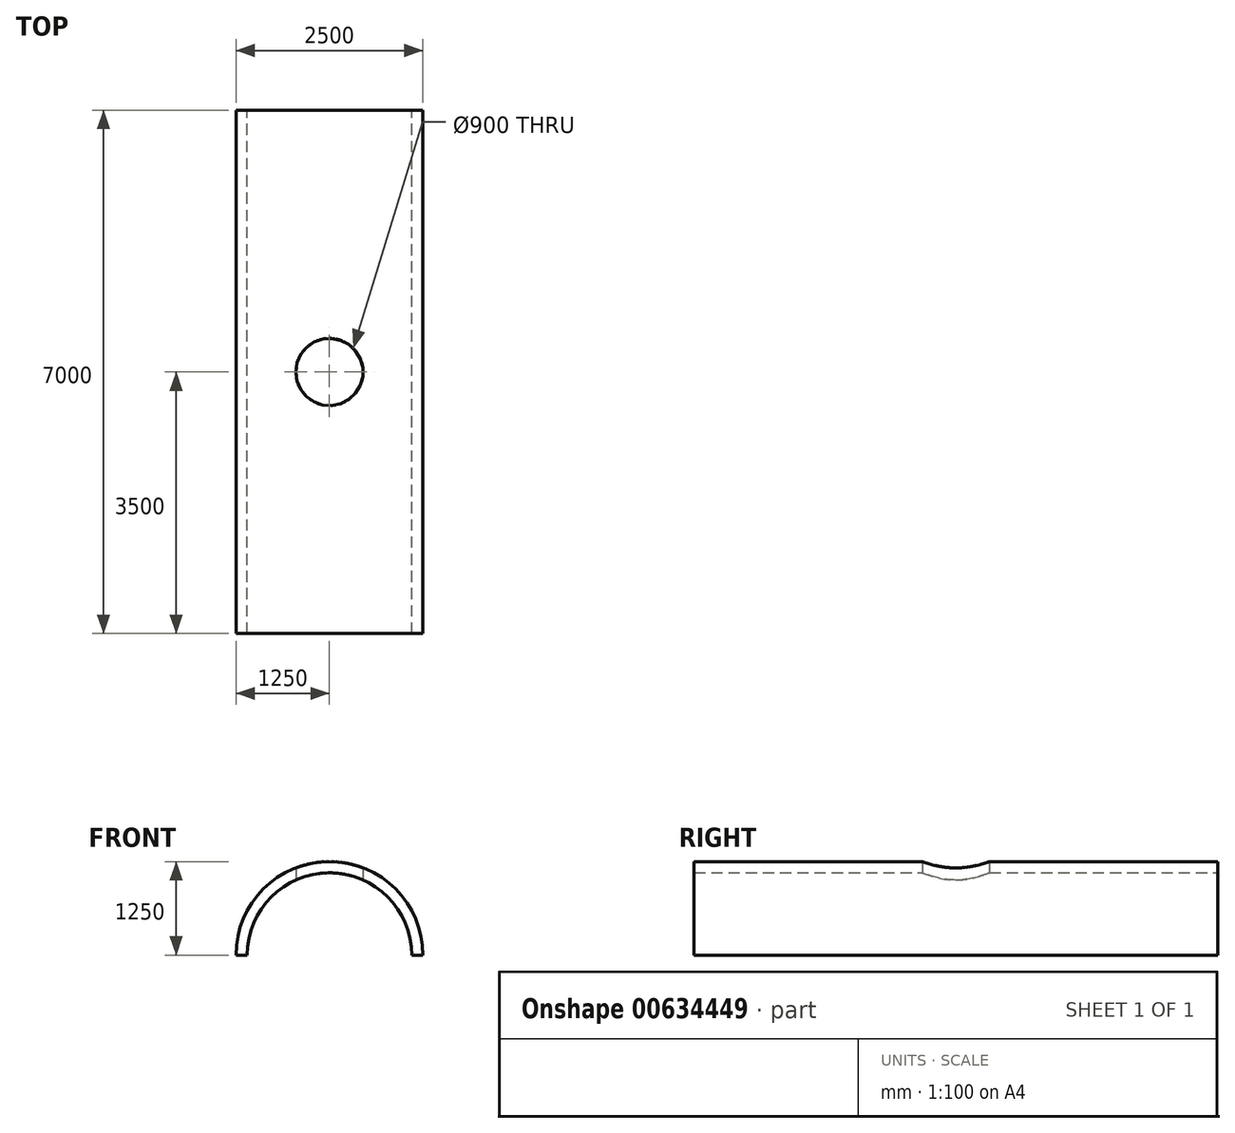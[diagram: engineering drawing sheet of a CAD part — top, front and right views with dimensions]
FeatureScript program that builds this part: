
annotation { "Feature Type Name" : "Feature", "Feature Type Description" : "" }
export const myFeature = defineFeature(function(context is Context, id is Id, definition is map)
    precondition{}
    {
        {
            var Q0;
            Q0=qCreatedBy(makeId("Front.planeOp"),FACE);
            var sketch = newSketch(context, id + "F0", { "sketchPlane" : qUnion([Q0])});
            skCircle(sketch, "E0", {"center": v(0, 0) * mm, "radius": 1250 * mm});
            skCircle(sketch, "E1", {"center": v(0, 0) * mm, "radius": 1100 * mm});
            skSolve(sketch);
        }
        {
            var Q0;
            Q0=makeQuery(id+"F0.imprint","IMPRINT",FACE,{"disambiguationData":[TD([[makeQuery(id+"F0.imprint","IMPRINT",EDGE,{"derivedFrom":sQuery(id+"F0.wireOp",EDGE,"E0")}),1.0]])]});
            extrude(context, id + "F1", {"entities" : qUnion([Q0]), "depth" : 7000 * mm, "offsetDistance" : 25 * mm});
        }
        {
            var Q0;
            Q0=qCreatedBy(makeId("Front.planeOp"),FACE);
            var sketch = newSketch(context, id + "F2", { "sketchPlane" : qUnion([Q0])});
            skLineSegment(sketch, "E2.bottom", {"start": v(-1995.14, 0) * mm, "end": v(2355.4, 0) * mm});
            skLineSegment(sketch, "E2.top", {"start": v(-1995.14, -1751.12) * mm, "end": v(2355.4, -1751.12) * mm});
            skLineSegment(sketch, "E2.left", {"start": v(-1995.14, 0) * mm, "end": v(-1995.14, -1751.12) * mm});
            skLineSegment(sketch, "E2.right", {"start": v(2355.4, 0) * mm, "end": v(2355.4, -1751.12) * mm});
            skSolve(sketch);
        }
        {
            var Q0;
            Q0=makeQuery(id+"F2.imprint","IMPRINT",FACE,{"disambiguationData":[TD([[makeQuery(id+"F2.imprint","IMPRINT",EDGE,{"derivedFrom":sQuery(id+"F2.wireOp",EDGE,"E2.bottom")}),-1.0]])]});
            extrude(context, id + "F3", {"entities" : qUnion([Q0]), "operationType" : NewBodyOperationType.REMOVE, "depth" : 8000 * mm, "offsetDistance" : 25 * mm});
        }
        {
            var Q0;
            Q0=qCreatedBy(makeId("Top.planeOp"),FACE);
            var sketch = newSketch(context, id + "F4", { "sketchPlane" : qUnion([Q0])});
            skCircle(sketch, "E3", {"center": v(0, -3500) * mm, "radius": 450 * mm});
            skSolve(sketch);
        }
        {
            var Q0;
            Q0=makeQuery(id+"F4.imprint","IMPRINT",FACE,{"disambiguationData":[TD([[makeQuery(id+"F4.imprint","IMPRINT",EDGE,{"derivedFrom":sQuery(id+"F4.wireOp",EDGE,"E3")}),1.0]])]});
            var Q1;
            Q1=sQuery(id+"F4.wireOp",EDGE,"E3");
            extrude(context, id + "F5", {"entities" : qUnion([Q0]), "operationType" : NewBodyOperationType.REMOVE, "surfaceEntities" : qUnion([Q1]), "depth" : 10000 * mm, "offsetDistance" : 25 * mm});
        }
    });
